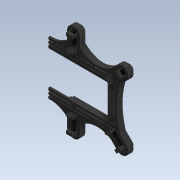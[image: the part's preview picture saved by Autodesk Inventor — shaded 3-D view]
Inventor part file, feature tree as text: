
AUTODESK INVENTOR PART (.ipt)
format: ipt  version: 2020 (Build 240168000, 168)  size: 2,973,184 bytes
history: native  units: mm
features: projected_geometry x47, extrude x36, sketch x36, reference x22, other x20, chamfer x10, plane x4, hole x3, move_body x3, direct_edit x2
ambient origin geometry x8: Origin, YZ Plane, XZ Plane, XY Plane, X Axis, Y Axis, Z Axis, Center Point
bodies: Solid1 (feature_tree)
feature tree (183):
  extrude  "Extrusion1"  Depth=50.0mm
  extrude  "Extrusion2"  Depth=22.0mm
  extrude  "Extrusion3"  Depth=35.3mm
  hole  "Hole2"  [1 undecoded]
  extrude  "Extrusion10"  Depth=19.0mm
  extrude  "Extrusion17"  Depth=10.0mm
  sketch  "Sketch27"  dims[d12=19.0mm d13=100.0mm]
  hole  "Hole4"  [1 undecoded]
  extrude  "Extrusion29"  Depth=17.453293mm
  extrude  "Extrusion30"  Depth=13.962634mm
  extrude  "Extrusion31"  Depth=4.8mm
  extrude  "Extrusion34"  Depth=6.2mm
  plane  "Work Plane1"
  extrude  "Extrusion42"  Depth=2.5mm
  hole  "Hole6"  [1 undecoded]
  extrude  "Extrusion46"  Depth=2.0mm
  chamfer  "Chamfer13"  Distance=4.8mm
  chamfer  "Chamfer14"  Distance=33.0mm
  chamfer  "Chamfer15"  Distance=2.5mm
  chamfer  "Chamfer16"  Distance=2.0mm
  chamfer  "Chamfer17"  Distance=2.5mm
  chamfer  "Chamfer18"  Distance=2.0mm
  extrude  "Extrusion54"  Depth=0.5mm
  chamfer  "Chamfer19"  Distance=2.0mm
  extrude  "Extrusion55"  Depth=0.5mm
  plane  "Work Plane2"
  extrude  "Extrusion57"  Depth=0.5mm
  direct_edit  "Direct Edit5"
  direct_edit  "Direct Edit6"
  plane  "Work Plane3"
  extrude  "Extrusion58"  Depth=10.0mm TaperAngle=0.0deg
  sketch  "Sketch59"  dims[d30=6.2mm]
  extrude  "Extrusion59"  Depth=0.5mm
  extrude  "Extrusion60"  Depth=0.5mm
  chamfer  "Chamfer21"  Distance=207.691804mm
  extrude  "Extrusion61"  Depth=0.5mm
  extrude  "Extrusion62"  Depth=0.5mm
  extrude  "Extrusion63"  Depth=12.4mm
  extrude  "Extrusion64"  Depth=0.5mm
  sketch  "Sketch65"  dims[d37=6.2mm]
  plane  "Work Plane4"
  extrude  "Extrusion65"  Depth=12.4mm
  extrude  "Extrusion66"  Depth=0.5mm
  extrude  "Extrusion68"  Depth=0.5mm
  extrude  "Extrusion69"  Depth=0.5mm
  extrude  "Extrusion71"  Depth=0.5mm
  extrude  "Extrusion84"  Depth=0.5mm TaperAngle=0.0deg
  extrude  "Extrusion85"  Depth=5.0mm TaperAngle=0.0deg
  chamfer  "Chamfer24"  Distance=5.0mm
  extrude  "Extrusion86"  Depth=0.5mm
  extrude  "Extrusion87"  Depth=0.5mm
  extrude  "Extrusion88"  Depth=0.5mm TaperAngle=0.0deg
  extrude  "Extrusion89"  Depth=0.5mm TaperAngle=0.0deg
  extrude  "Extrusion90"  Depth=0.5mm
  extrude  "Extrusion91"  Depth=0.5mm
  chamfer  "Chamfer25"  Distance=4.5mm
  extrude  "Extrusion92"  Depth=0.5mm
  extrude  "Extrusion93"  Depth=12.4mm
  sketch  "Sketch1"  dims[d0=50.0mm d1=4.404mm]
  reference  "Reference1"
  reference  "Reference2"
  reference  "Reference3"
  reference  "Reference4"
  sketch  "Sketch2"  dims[d2=135.0deg d3=22.0mm]
  reference  "Reference5"
  reference  "Reference6"
  reference  "Reference7"
  reference  "Reference8"
  reference  "Reference9"
  reference  "Reference10"
  reference  "Reference11"
  reference  "Reference12"
  reference  "Reference13"
  reference  "Reference14"
  reference  "Reference15"
  reference  "Reference16"
  sketch  "Sketch3"  dims[d4=35.3mm d5=35.3mm]
  projected_geometry  "Projected Loop1"
  projected_geometry  "Projected Loop2"
  sketch  "Sketch6"  dims[d6=98.287843mm d7=10.0mm]
  reference  "Reference23"
  reference  "Reference24"
  reference  "Reference25"
  reference  "Reference26"
  reference  "Reference27"
  reference  "Reference28"
  sketch  "Sketch13"  dims[d8=19.0mm d9=19.0mm]
  sketch  "Sketch18"  dims[d10=6.0mm d11=10.0mm]
  projected_geometry  "Projected Loop13"
  projected_geometry  "Projected Loop19"
  projected_geometry  "Projected Loop23"
  projected_geometry  "Projected Loop28"
  projected_geometry  "Projected Loop29"
  projected_geometry  "Projected Loop30"
  projected_geometry  "Projected Loop33"
  sketch  "Sketch31"  dims[d14=30.0mm d15=17.453293mm]
  projected_geometry  "Projected Loop34"
  sketch  "Sketch32"  dims[d16=30.0mm d17=13.962634mm]
  projected_geometry  "Projected Loop35"
  projected_geometry  "Projected Loop36"
  projected_geometry  "Projected Loop37"
  projected_geometry  "Projected Loop38"
  projected_geometry  "Projected Loop39"
  projected_geometry  "Projected Loop40"
  projected_geometry  "Projected Loop41"
  projected_geometry  "Projected Loop42"
  projected_geometry  "Projected Loop43"
  projected_geometry  "Projected Loop44"
  projected_geometry  "Projected Loop45"
  projected_geometry  "Projected Loop46"
  sketch  "Sketch35"  dims[d18=2.0mm d19=4.8mm]
  projected_geometry  "Projected Loop52"
  sketch  "Sketch42"  dims[d20=6.2mm d21=6.2mm]
  projected_geometry  "Projected Loop61"
  projected_geometry  "Projected Loop62"
  sketch  "Sketch46"  dims[d22=33.0mm d23=2.5mm]
  sketch  "Sketch54"  dims[d24=2.0mm d25=2.5mm]
  projected_geometry  "Projected Loop74"
  sketch  "Sketch55"  dims[d26=2.0mm d27=2.0mm]
  sketch  "Sketch57"  dims[d28=90.0deg]
  projected_geometry  "Projected Loop76"
  sketch  "Sketch58"  dims[d29=6.2mm]
  projected_geometry  "Projected Loop77"
  projected_geometry  "Projected Loop78"
  sketch  "Sketch60"  dims[d31=33.0mm]
  projected_geometry  "Projected Loop79"
  projected_geometry  "Projected Loop80"
  sketch  "Sketch61"  dims[d32=2.0mm]
  sketch  "Sketch62"  dims[d33=2.5mm]
  projected_geometry  "Projected Loop81"
  sketch  "Sketch63"  dims[d35=2.0mm]
  sketch  "Sketch64"  dims[d36=4.8mm]
  projected_geometry  "Projected Loop82"
  projected_geometry  "Projected Loop83"
  sketch  "Sketch66"  dims[d38=6.2mm]
  sketch  "Sketch68"  dims[d39=33.0mm]
  projected_geometry  "Projected Loop85"
  projected_geometry  "Projected Loop86"
  sketch  "Sketch69"  dims[d40=2.5mm]
  sketch  "Sketch71"  dims[d41=2.0mm]
  projected_geometry  "Projected Loop88"
  sketch  "Sketch85"  dims[d42=2.5mm]
  projected_geometry  "Projected Loop108"
  sketch  "Sketch86"  dims[d43=2.0mm]
  projected_geometry  "Projected Loop109"
  sketch  "Sketch87"  dims[d44=2.0mm]
  sketch  "Sketch88"  dims[d45=2.5mm]
  projected_geometry  "Projected Loop110"
  sketch  "Sketch89"  dims[d46=19.402mm]
  projected_geometry  "Projected Loop111"
  sketch  "Sketch90"  dims[d47=169.440339mm]
  projected_geometry  "Projected Loop112"
  sketch  "Sketch91"  dims[d48=155.440339mm]
  projected_geometry  "Projected Loop113"
  projected_geometry  "Projected Loop114"
  projected_geometry  "Projected Loop115"
  sketch  "Sketch93"  dims[d58=2.0mm]
  projected_geometry  "Projected Loop116"
  sketch  "Sketch94"  dims[d59=2.0mm d71=4.8mm d72=33.0mm d73=2.5mm d74=2.0mm d75=2.5mm d76=2.0mm d77=14.0mm d78=2.0mm d79=106.731156mm d80=94.331156mm d81=10.0mm d82=0.0mm d83=146.583126mm d84=113.583126mm d85=207.691804mm d86=235.691804mm d87=89.108678mm d88=12.4mm d89=56.108678mm d90=12.4mm d91=23.0mm d92=142.600153mm d93=170.600153mm d94=142.600153mm d95=19.0mm d96=0.0mm d97=5.0mm d98=0.0mm d153=10.0mm d154=6.0mm d155=4.0mm d156=2.0mm d157=90.0deg d158=3.8mm d159=0.0mm d207=5.0mm d208=22.5mm d209=45.0mm d210=25.0mm d211=0.0mm d310=9.0mm d311=0.0mm d382=2.0mm d383=6.0mm d384=4.0mm d385=2.0mm d386=90.0deg d387=10.0mm d388=0.0mm d455=6.0mm d456=4.5mm d457=4.5mm d458=1.7mm d459=12.4mm d460=6.0mm d461=4.5mm d462=4.5mm d463=6.0mm d464=4.5mm d465=4.5mm d466=6.0mm d467=4.5mm d468=4.5mm d472=6.0mm d473=4.5mm d474=4.5mm d475=4.5mm d476=4.5mm d477=6.0mm d478=154.585126mm d479=147.583126mm d480=147.583126mm d481=9.0mm d482=0.0mm d483=154.585126mm d484=90.108678mm d485=10.7mm d486=147.583126mm d487=66.300077mm d488=72.372447mm d489=10.0mm d490=0.0mm d491=0.0mm d492=231.691804mm d493=91.808678mm d494=139.883126mm d495=171.600153mm d496=1.7mm d497=5.0mm d498=0.0mm d523=138.2mm d524=45.2mm d525=22.6mm d526=69.1mm d529=10.0mm d530=0.0mm d590=8.0mm d591=0.0mm d592=2.0mm d593=6.0mm d594=4.0mm d595=2.0mm d596=90.0deg d597=6.5mm d598=0.0mm d669=2.4mm d670=0.0mm d696=4.75mm d697=10.0mm d698=45.0deg d699=4.75mm d700=10.0mm d701=45.0deg d702=4.75mm d703=10.0mm d704=45.0deg d705=4.75mm d706=10.0mm d707=45.0deg d708=4.75mm d709=10.0mm d710=45.0deg d711=4.75mm d712=10.0mm d713=45.0deg d716=4.0mm d717=91.5mm d718=0.0mm d721=2.0mm d722=2.0mm d723=45.0deg d725=5.0mm d726=0.0mm d729=70.0mm d730=135.0deg d731=30.0deg d732=17.3mm d733=135.0deg d734=55.0mm d735=0.0mm d757=0.0mm d758=0.0mm d759=4.0mm d760=0.0mm d761=0.0mm d762=4.0mm d763=0.0mm d764=0.0mm d765=3.025mm d766=0.0mm d767=4.0mm d768=4.0mm d769=40.876479mm d770=46.75mm d771=0.0mm d772=103.75mm d773=0.0mm d774=206.25mm d775=0.0mm d776=4.0mm d777=2.0mm d778=45.0deg d779=12.0mm d780=4.0mm d781=120.0mm d782=15.0mm d785=120.0mm d786=12.0mm d787=15.0mm d788=41.75mm d789=0.0mm d790=3.0mm d791=0.0mm d792=3.0mm d794=3.0mm d795=3.0mm d796=8.0mm d797=0.0mm d805=4.0mm d806=0.0mm d807=0.2mm d808=0.2mm d809=0.2mm d810=0.2mm d811=46.75mm d812=0.0mm d813=63.0mm d814=0.0mm d847=3.7mm d848=3.7mm d849=3.7mm d850=3.7mm d851=3.7mm d852=3.7mm d853=50.0mm d854=50.0mm d855=50.0mm d856=50.0mm d857=10.0mm d858=0.0mm d859=10.0mm d860=0.0mm d867=10.0mm d868=0.0mm d931=5.0mm d932=0.0mm d933=5.515mm d934=7.012mm d935=3.0mm d936=5.515mm d937=7.012mm d938=3.0mm d939=10.0mm d940=0.0mm d941=5.0mm d942=2.0mm d943=45.0deg d944=7.0mm d945=2.015mm d946=7.0mm d947=7.0mm d948=7.0mm d949=34.913822mm d950=10.0mm d951=5.0mm d952=0.0mm d953=0.0mm d954=10.0mm d955=0.0mm d956=7.0mm d957=7.0mm d958=7.0mm d959=7.0mm d960=2.0mm d961=0.0mm d962=37.698mm d963=3.5mm d964=90.0deg d965=80.0mm d966=106.84198mm d967=133.75mm d968=84.5mm d969=0.0mm d970=0.0mm d971=133.75mm d972=0.0mm d973=6.0mm d974=5.0mm d975=10.0mm d976=3.0mm d977=10.0mm d978=5.0mm d979=10.0mm d980=3.0mm d981=10.0mm d982=7.0mm d984=10.0mm d985=3.0mm d986=10.0mm d987=4.0mm d988=10.0mm d989=3.0mm d990=10.0mm d991=4.0mm d994=5.0mm d995=10.0mm d996=3.0mm d997=10.0mm d998=5.0mm d999=10.0mm d1000=3.0mm d1001=10.0mm d1002=4.0mm d1003=4.0mm d1006=3.0mm d1007=0.0mm d1008=78.0mm d1009=3.0mm d1010=3.0mm d1011=9.0mm d1012=3.0mm d1013=5.0mm d1014=3.0mm d1015=3.0mm d1016=5.0mm d1017=3.0mm d1018=3.0mm d1019=5.0mm d1020=3.0mm d1021=5.200077mm d1024=5.200077mm d1026=12.200077mm d1028=33.200077mm d1030=49.200077mm d1031=4.0mm d1032=3.0mm d1033=17.0mm d1034=3.0mm d1036=4.0mm d1037=3.0mm d1038=4.0mm d1039=2.0mm d1040=3.0mm d1041=5.0mm d1042=4.0mm d1043=8.0mm d1044=3.0mm d1045=21.0mm d1046=4.0mm d1047=3.0mm d1048=4.0mm d1049=7.0mm d1050=3.0mm d1051=4.0mm d1052=6.0mm d1053=3.0mm d1054=4.0mm d1055=2.0mm d1056=3.0mm d1057=3.5mm d1058=1.5mm d1059=3.0mm d1060=1.5mm d1061=1.5mm d1062=1.0mm d1063=2.0mm d1064=45.0deg d1065=5.2mm d1066=44.0mm d1067=3.0mm d1068=4.0mm d1069=8.0mm d1070=3.0mm d1071=12.0mm d1072=1.5mm d1073=1.5mm d1074=3.0mm d1075=88.415041mm d1076=1.2mm d1077=1.5mm d1078=3.0mm d1079=68.0mm d1080=3.0mm d1081=3.0mm d1082=22.0mm d1083=14.0mm d1084=3.0mm d1085=26.0mm d1086=3.0mm d1087=2.0mm d1088=1.5mm d1089=10.0mm d1090=3.0mm d1091=1.5mm d1092=3.0mm d1093=1.5mm d1094=10.0mm d1095=3.0mm d1096=1.5mm d1097=3.0mm d1098=1.5mm d1099=10.0mm d1100=3.0mm d1101=1.5mm d1102=3.0mm d1103=1.5mm d1104=10.0mm d1105=3.0mm d1106=1.5mm d1107=3.0mm d1108=1.5mm d1109=3.5mm d1110=3.5mm d1111=3.5mm d1112=18.9mm d1113=36.456379mm d1114=31.860185mm d1115=27.26399mm d1116=3.0mm d1117=0.0mm d1118=11.0mm d1119=11.0mm d1120=11.0mm d1121=11.0mm d1122=3.8mm d1123=0.0mm d99=0.5mm d100=0.872665mm d160=0.5mm d161=0.872665mm d162=0.5mm d163=0.872665mm d171=0.5mm d172=0.872665mm d173=0.5mm d174=0.872665mm d191=0.5mm d192=0.872665mm d193=0.5mm d194=0.872665mm d205=0.5mm d206=0.872665mm d244=0.5mm d245=0.872665mm d246=0.5mm d247=0.872665mm d307=0.5mm d308=0.872665mm d309=0.5mm d352=0.5mm d353=0.872665mm d354=0.5mm d355=0.872665mm d412=0.5mm d413=0.872665mm d414=0.5mm d415=0.872665mm d416=0.5mm d417=0.872665mm d586=0.5mm d587=0.872665mm d588=0.5mm d589=0.872665mm d861=0.5mm d862=0.872665mm d905=0.5mm d906=0.872665mm d907=0.5mm d908=0.872665mm]
  projected_geometry  "Projected Loop117"
  other  "<userpath>\Documents\Inventor Projects\SpiderTest\Test3\SpiderLegDemo.iam"
  other  "SpiderLegDemo.iam"
  other  "Tower Pro MG90S Micro servo:1"
  other  "Крышка корпуса задняя:1"
  other  "Крышка корпуса:1"
  other  "LegSup:1"
  other  "<userpath>\Documents\Inventor Projects\SpiderTest\Test5\Demo.iam"
  other  "Demo.iam"
  other  "SpiderLegDemoRight:1"
  other  "SpiderLegDemoRight:5"
  other  "<userpath>\Documents\Inventor Projects\SpiderTest\Test3\Demo.iam"
  other  "SpiderLegDemo:3"
  other  "SpiderLegDemo:4"
  other  "SpiderLegDemo:2"
  other  "SpiderLegDemoRight:6"
  other  "SpiderLegDemoLeft:2"
  other  "Вал последний с чем то:1"
  other  "SpiderLegDemoLeft:3"
  other  "ограничитель:2"
  other  "SpiderLegDemoLeft:1"
  move_body  "Move7"
  move_body  "Move8"
  move_body  "Move9"
note: 3 required parameter values undecoded (feature->parameter linkage not recoverable at this tier; creation-order binding heuristic only, values carry confidence <= 0.55)
